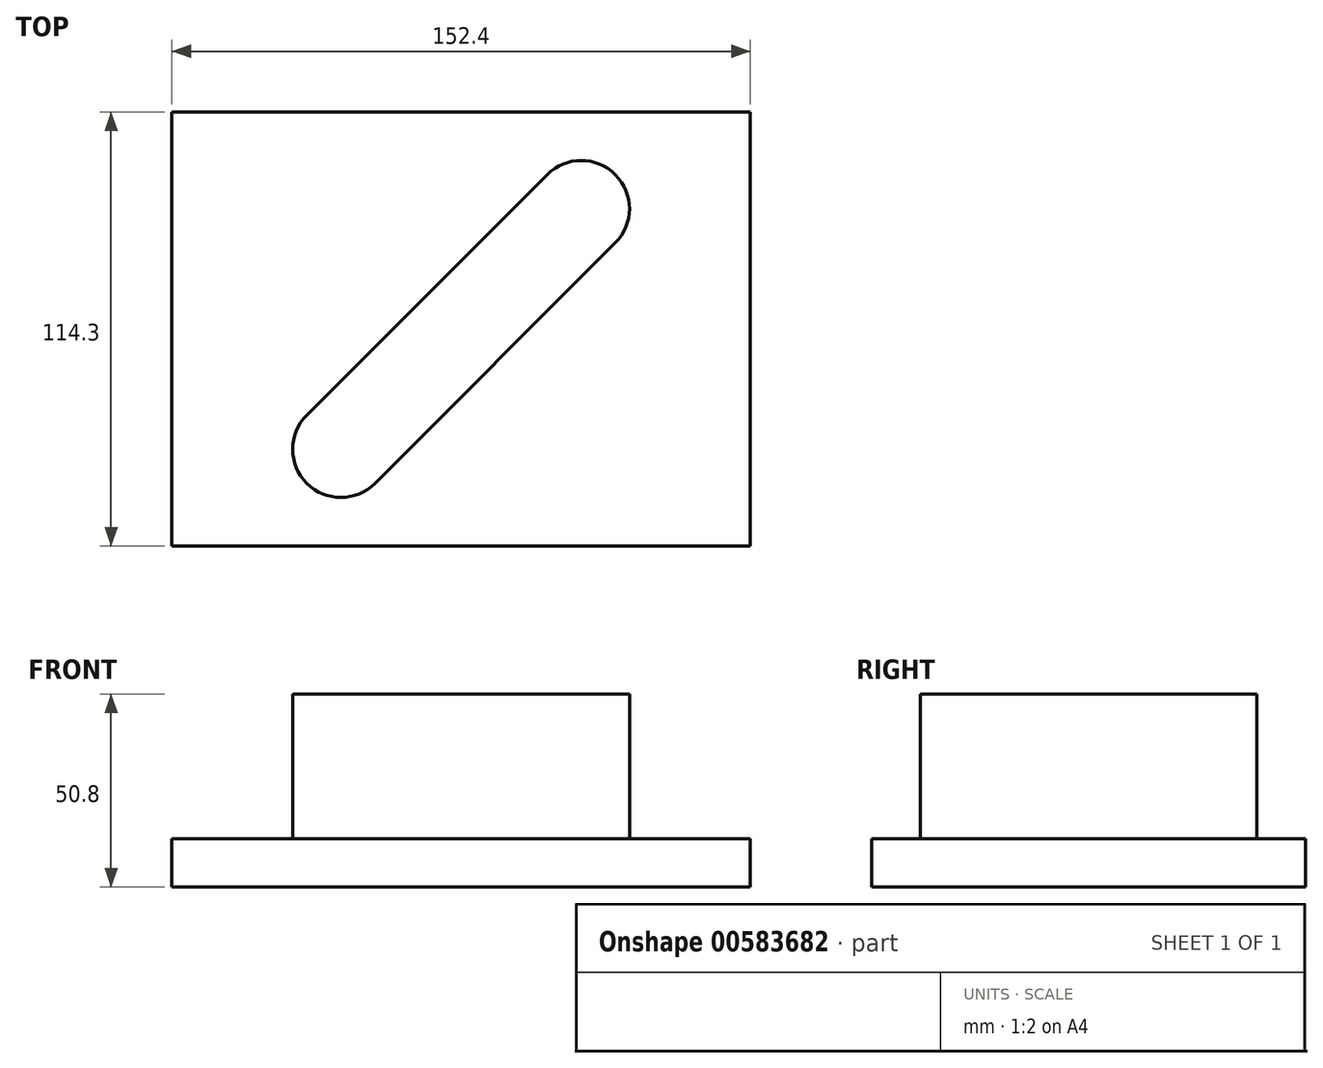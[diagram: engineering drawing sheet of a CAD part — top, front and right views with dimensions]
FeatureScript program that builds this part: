
annotation { "Feature Type Name" : "Feature", "Feature Type Description" : "" }
export const myFeature = defineFeature(function(context is Context, id is Id, definition is map)
    precondition{}
    {
        {
            var Q0;
            Q0=qCreatedBy(makeId("Top.planeOp"),FACE);
            var sketch = newSketch(context, id + "F0", { "sketchPlane" : qUnion([Q0])});
            skLineSegment(sketch, "E0.bottom", {"start": v(-152.4, 114.3) * mm, "end": v(0, 114.3) * mm});
            skLineSegment(sketch, "E0.top", {"start": v(-152.4, 0) * mm, "end": v(0, 0) * mm});
            skLineSegment(sketch, "E0.left", {"start": v(-152.4, 114.3) * mm, "end": v(-152.4, 0) * mm});
            skLineSegment(sketch, "E0.right", {"start": v(0, 114.3) * mm, "end": v(0, 0) * mm});
            skSolve(sketch);
        }
        {
            var Q0;
            Q0 = qSketchRegion(id + "F0", true);
            extrude(context, id + "F1", {"entities" : qUnion([Q0]), "depth" : 12.7 * mm, "offsetDistance" : 25.4 * mm, "symmetric" : true});
        }
        {
            var Q0;
            Q0=makeQuery(id+"F1.opExtrude","CAP_FACE",FACE,{"disambiguationData":[OSD([sQuery(id+"F0.wireOp",EDGE,"E0.bottom"),sQuery(id+"F0.wireOp",EDGE,"E0.top"),sQuery(id+"F0.wireOp",EDGE,"E0.left"),sQuery(id+"F0.wireOp",EDGE,"E0.right")])],"isStart":false});
            var sketch = newSketch(context, id + "F2", { "sketchPlane" : qUnion([Q0])});
            skLineSegment(sketch, "E1", {"start": v(-76.2, 114.3) * mm, "end": v(-76.2, 0) * mm, "construction": true});
            skLineSegment(sketch, "E2", {"start": v(-107.86, 25.5) * mm, "end": v(-76.2, 57.15) * mm, "construction": true});
            skLineSegment(sketch, "E3", {"start": v(-76.2, 57.15) * mm, "end": v(-44.54, 88.8) * mm, "construction": true});
            skLineSegment(sketch, "E4", {"start": v(-116.84, 34.47) * mm, "end": v(-107.86, 25.5) * mm});
            skLineSegment(sketch, "E5", {"start": v(-98.88, 16.51) * mm, "end": v(-107.86, 25.5) * mm});
            skLineSegment(sketch, "E6", {"start": v(-44.54, 88.8) * mm, "end": v(-35.56, 79.83) * mm});
            skLineSegment(sketch, "E7", {"start": v(-35.56, 79.83) * mm, "end": v(-98.88, 16.51) * mm});
            skLineSegment(sketch, "E8", {"start": v(-44.54, 88.8) * mm, "end": v(-53.52, 97.79) * mm});
            skLineSegment(sketch, "E9", {"start": v(-53.52, 97.8) * mm, "end": v(-116.84, 34.47) * mm});
            skArc(sketch, "E10", {"start": v(-53.52, 97.79) * mm, "mid": v(-35.56, 97.79) * mm, "end": v(-35.56, 79.83) * mm});
            skArc(sketch, "E11", {"start": v(-98.88, 16.51) * mm, "mid": v(-116.84, 16.51) * mm, "end": v(-116.84, 34.47) * mm});
            skLineSegment(sketch, "E12", {"start": v(-44.54, 88.8) * mm, "end": v(-35.56, 97.79) * mm, "construction": true});
            skLineSegment(sketch, "E13", {"start": v(-107.86, 25.5) * mm, "end": v(-116.84, 16.51) * mm, "construction": true});
            skSolve(sketch);
        }
        {
            var Q0;
            Q0 = qSketchRegion(id + "F2", true);
            extrude(context, id + "F3", {"entities" : qUnion([Q0]), "operationType" : NewBodyOperationType.ADD, "depth" : 38.1 * mm, "offsetDistance" : 25.4 * mm});
        }
    });
